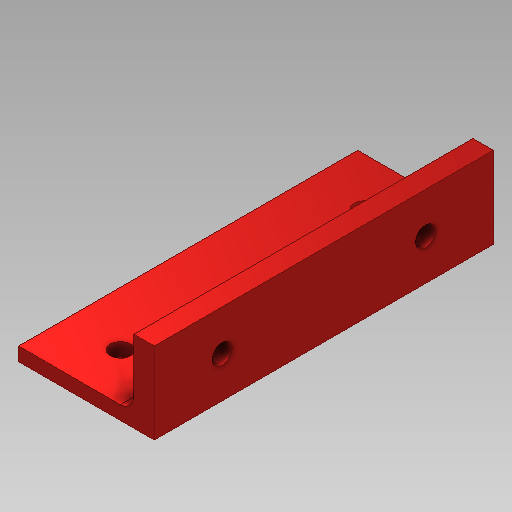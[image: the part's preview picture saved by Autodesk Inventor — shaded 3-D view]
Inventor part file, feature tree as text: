
AUTODESK INVENTOR PART (.ipt)
format: ipt  version: 2020 (Build 240168000, 168)  size: 145,408 bytes
history: native  units: in
note: dims shown in document units (in); Inventor stores cm internally (conversion verified against a paired STEP export)
features: extrude x3, sketch x3, fillet x1
ambient origin geometry x8: Origin, YZ Plane, XZ Plane, XY Plane, X Axis, Y Axis, Z Axis, Center Point
bodies: Solid1 (feature_tree)
feature tree (7):
  extrude  "Extrusion1"  Depth=1.9685in
  extrude  "Extrusion2"  Depth=1.4173in
  extrude  "Extrusion3"  Depth=0.0787in
  fillet  "Fillet1"  Radius=0.1181in
  sketch  "Sketch1"  dims[d0=0.7874in d1=1.9685in]
  sketch  "Sketch2"  dims[d2=0.7087in d3=1.4173in]
  sketch  "Sketch3"  dims[d4=0.0787in d5=0.0787in d6=0.1181in d7=0.1181in d8=0.0787in d9=0.0in d10=0.1181in d11=0.3937in d12=0.0in d13=0.2362in d14=0.7874in d15=0.7874in d16=0.7874in d17=0.1969in d18=1.1811in d19=0.1181in d20=0.1181in d21=0.3937in d22=0.0in d23=0.0787in]
